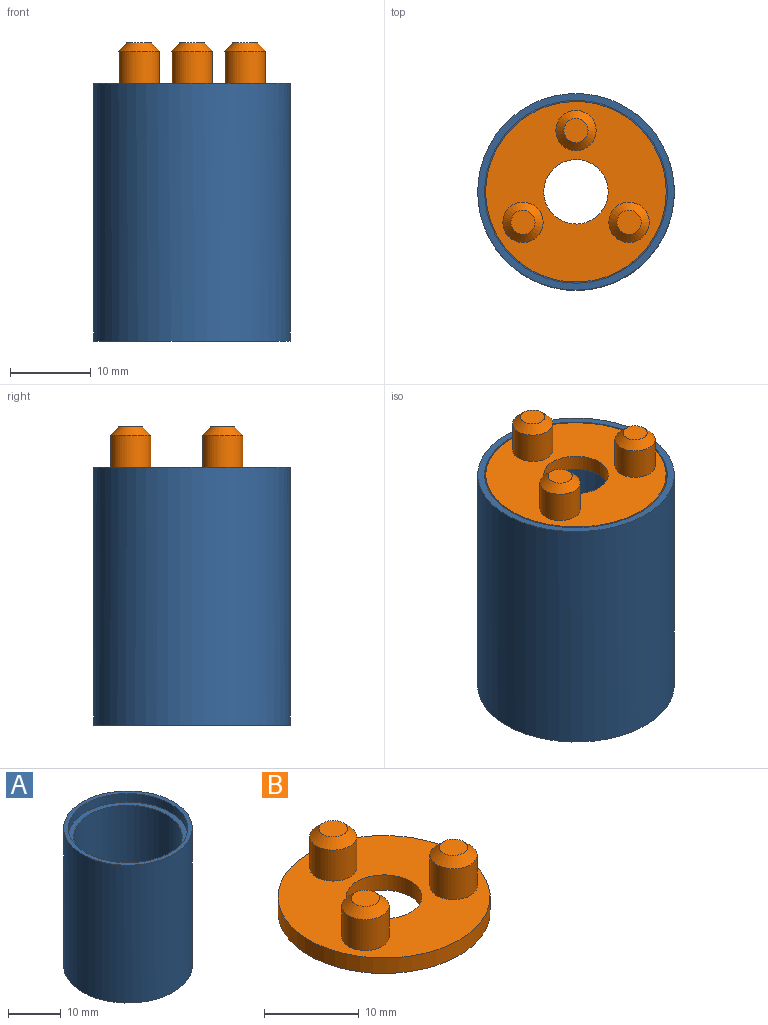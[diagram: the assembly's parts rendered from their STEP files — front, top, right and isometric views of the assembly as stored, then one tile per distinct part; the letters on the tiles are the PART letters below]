
ASSEMBLY  parts=2 mates=1
PART A: 6 faces, bbox 24.4x24.4x32 mm
  f0: cylinder r=12.2mm len=32mm, axis (0,0,-1), area 2453mm2, adj f3,f5
  f1: cylinder r=10.3mm len=30mm, axis (0,0,-1), area 1941.5mm2, adj f2,f5
  f2: plane 22.7x22.7mm, normal (0,0,1), area 71.4mm2, adj f1,f4
  f3: plane 24.4x24.4mm, normal (0,0,1), area 62.9mm2, adj f0,f4
  f4: cylinder r=11.35mm len=22.7mm, axis (0,0,-1), area 142.6mm2, adj f2,f3
  f5: plane 24.4x24.4mm, normal (0,0,-1), area 134.3mm2, adj f0,f1
PART B: 13 faces, bbox 22.4x22.4x7 mm
  f0: cylinder r=11.2mm len=22.4mm, axis (0,0,-1), area 140.7mm2, adj f1,f2
  f1: plane 22.4x22.4mm, normal (0,0,1), area 284.9mm2, adj f0,f3,f4,f6,f8
  f2: plane 22.4x22.4mm, normal (0,0,-1), area 343.8mm2, adj f0,f3
  f3: cylinder r=4mm len=8mm, axis (0,0,-1), area 50.3mm2, adj f1,f2
  f4: cylinder r=2.5mm len=5mm, axis (0,0,-1), area 62.8mm2, adj f1,f12
  f5: plane 3x3mm, normal (0,0,1), area 7.1mm2, adj f12
  f6: cylinder r=2.5mm len=5mm, axis (0,0,-1), area 62.8mm2, adj f1,f11
  f7: plane 3x3mm, normal (0,0,1), area 7.1mm2, adj f11
  f8: cylinder r=2.5mm len=5mm, axis (0,0,-1), area 62.8mm2, adj f1,f10
  f9: plane 3x3mm, normal (0,0,1), area 7.1mm2, adj f10
  f10: cone r=1.5mm half-angle=45deg, axis (0,0,-1), area 17.8mm2, adj f8,f9
  f11: cone r=1.5mm half-angle=45deg, axis (0,0,-1), area 17.8mm2, adj f6,f7
  f12: cone r=1.5mm half-angle=45deg, axis (0,0,-1), area 17.8mm2, adj f4,f5
PLACE A t=(0.94,-43.77,4.45)mm
PLACE B t=(0.94,-43.77,4.45)mm
MATE fastened B.f0 <-> A.f0  axis (0,0,-1) through (-48.81,5.98,51.45)mm
